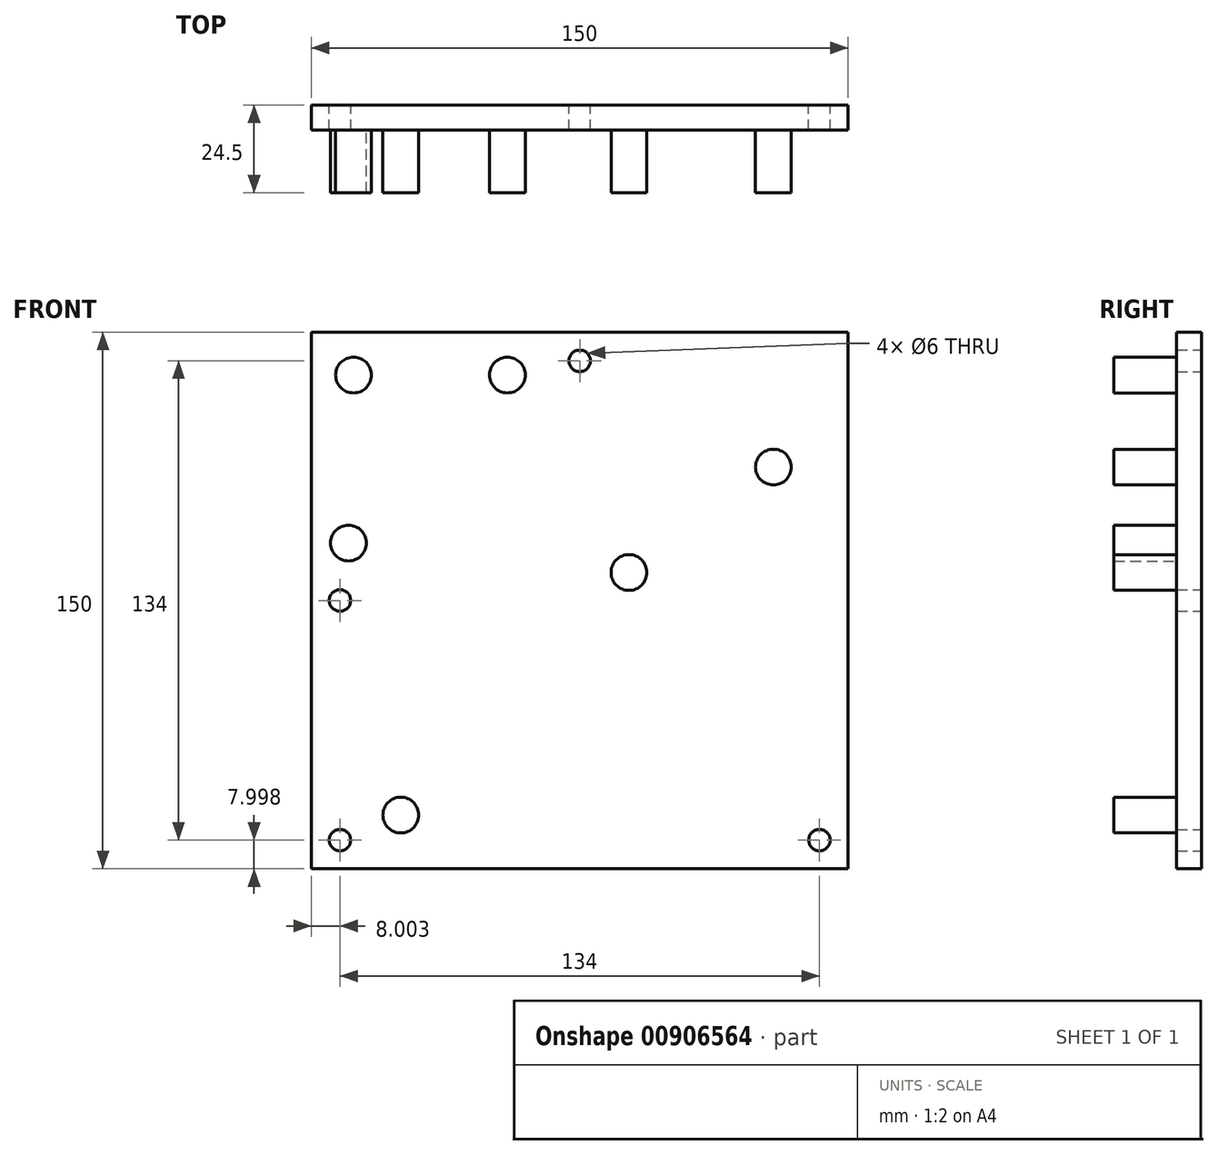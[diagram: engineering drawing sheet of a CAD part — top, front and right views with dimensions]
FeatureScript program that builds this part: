
annotation { "Feature Type Name" : "Feature", "Feature Type Description" : "" }
export const myFeature = defineFeature(function(context is Context, id is Id, definition is map)
    precondition{}
    {
        {
            var Q0;
            Q0=qCreatedBy(makeId("Front.planeOp"),FACE);
            var sketch = newSketch(context, id + "F0", { "sketchPlane" : qUnion([Q0])});
            skLineSegment(sketch, "E0.bottom", {"start": v(-68.6, -14.58) * mm, "end": v(81.4, -14.58) * mm});
            skLineSegment(sketch, "E0.top", {"start": v(-68.6, 135.42) * mm, "end": v(81.4, 135.42) * mm});
            skLineSegment(sketch, "E0.left", {"start": v(-68.6, -14.58) * mm, "end": v(-68.6, 135.42) * mm});
            skLineSegment(sketch, "E0.right", {"start": v(81.4, -14.58) * mm, "end": v(81.4, 135.42) * mm});
            skPoint(sketch, "E1", {"position": v(-68.6, 60.42) * mm});
            skPoint(sketch, "E2", {"position": v(6.4, -14.58) * mm});
            skLineSegment(sketch, "E3", {"start": v(6.4, -14.58) * mm, "end": v(6.4, 135.42) * mm, "construction": true});
            skCircle(sketch, "E4", {"center": v(6.4, 127.42) * mm, "radius": 3 * mm});
            skCircle(sketch, "E5", {"center": v(-60.6, -6.58) * mm, "radius": 3 * mm});
            skCircle(sketch, "E6", {"center": v(73.4, -6.58) * mm, "radius": 3 * mm});
            skCircle(sketch, "E7", {"center": v(-60.6, 60.42) * mm, "radius": 3 * mm});
            skSolve(sketch);
        }
        {
            var Q0;
            Q0 = qSketchRegion(id + "F0", true);
            extrude(context, id + "F1", {"entities" : qUnion([Q0]), "depth" : 7 * mm, "offsetDistance" : 25 * mm});
        }
        {
            var Q0;
            Q0=makeQuery(id+"F1.opExtrude","CAP_FACE",FACE,{"disambiguationData":[OSD([sQuery(id+"F0.wireOp",EDGE,"E0.bottom"),sQuery(id+"F0.wireOp",EDGE,"E0.top"),sQuery(id+"F0.wireOp",EDGE,"E0.left"),sQuery(id+"F0.wireOp",EDGE,"E0.right"),sQuery(id+"F0.wireOp",EDGE,"E4"),sQuery(id+"F0.wireOp",EDGE,"E5"),sQuery(id+"F0.wireOp",EDGE,"E6"),sQuery(id+"F0.wireOp",EDGE,"E7")])],"isStart":false});
            var sketch = newSketch(context, id + "F2", { "sketchPlane" : qUnion([Q0])});
            skCircle(sketch, "E8", {"center": v(-56.82, 123.45) * mm, "radius": 5 * mm});
            skCircle(sketch, "E9", {"center": v(-13.82, 123.45) * mm, "radius": 5 * mm});
            skCircle(sketch, "E10", {"center": v(-58.24, 76.48) * mm, "radius": 5 * mm});
            skCircle(sketch, "E11", {"center": v(-43.6, 0.42) * mm, "radius": 5 * mm});
            skCircle(sketch, "E12", {"center": v(20.16, 68.24) * mm, "radius": 5 * mm});
            skCircle(sketch, "E13", {"center": v(60.54, 97.72) * mm, "radius": 5 * mm});
            skSolve(sketch);
        }
        {
            var Q0;
            Q0 = qSketchRegion(id + "F2", true);
            extrude(context, id + "F3", {"entities" : qUnion([Q0]), "operationType" : NewBodyOperationType.ADD, "depth" : 17.5 * mm, "offsetDistance" : 25 * mm});
        }
    });
